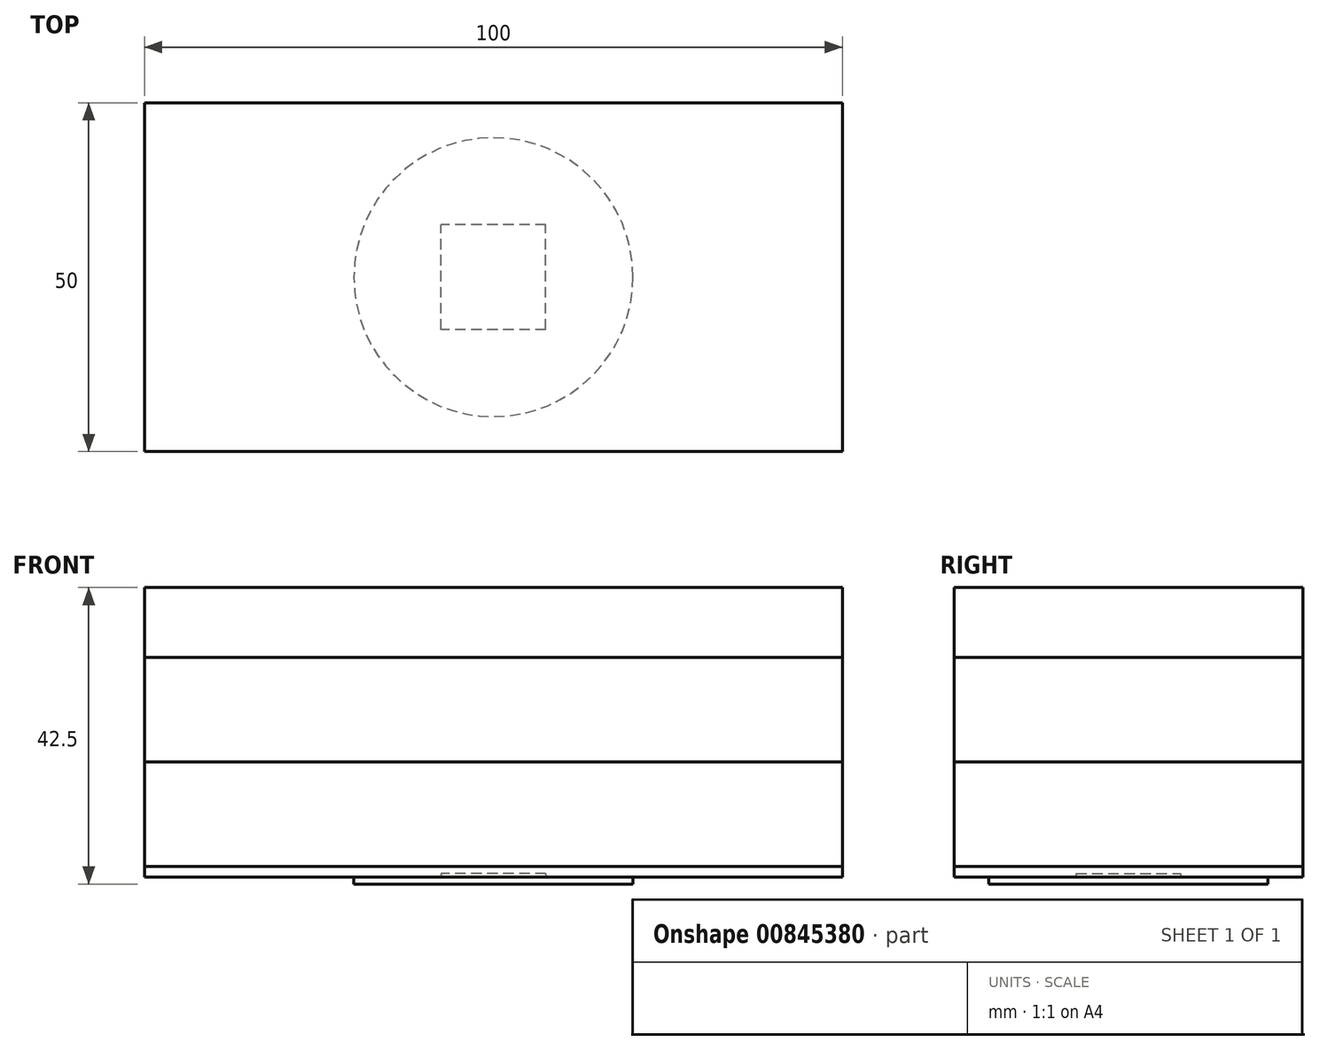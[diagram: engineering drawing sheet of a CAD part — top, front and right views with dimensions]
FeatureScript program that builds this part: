
annotation { "Feature Type Name" : "Feature", "Feature Type Description" : "" }
export const myFeature = defineFeature(function(context is Context, id is Id, definition is map)
    precondition{}
    {
        {
            var Q0;
            Q0=qCreatedBy(makeId("Top.planeOp"),FACE);
            var sketch = newSketch(context, id + "F0", { "sketchPlane" : qUnion([Q0])});
            skLineSegment(sketch, "E0.bottom", {"start": v(7.5, -7.5) * mm, "end": v(-7.5, -7.5) * mm});
            skLineSegment(sketch, "E0.top", {"start": v(7.5, 7.5) * mm, "end": v(-7.5, 7.5) * mm});
            skLineSegment(sketch, "E0.left", {"start": v(7.5, -7.5) * mm, "end": v(7.5, 7.5) * mm});
            skLineSegment(sketch, "E0.right", {"start": v(-7.5, -7.5) * mm, "end": v(-7.5, 7.5) * mm});
            skPoint(sketch, "E0.middle", {"position": v(0, 0) * mm});
            skSolve(sketch);
        }
        {
            var Q0;
            Q0 = qSketchRegion(id + "F0", true);
            extrude(context, id + "F1", {"entities" : qUnion([Q0]), "depth" : 0.5 * mm, "offsetDistance" : 25 * mm});
        }
        {
            var Q0;
            Q0=qCreatedBy(makeId("Top.planeOp"),FACE);
            var sketch = newSketch(context, id + "F2", { "sketchPlane" : qUnion([Q0])});
            skLineSegment(sketch, "E1.bottom", {"start": v(50, 25) * mm, "end": v(-50, 25) * mm});
            skLineSegment(sketch, "E1.top", {"start": v(50, -25) * mm, "end": v(-50, -25) * mm});
            skLineSegment(sketch, "E1.left", {"start": v(50, 25) * mm, "end": v(50, -25) * mm});
            skLineSegment(sketch, "E1.right", {"start": v(-50, 25) * mm, "end": v(-50, -25) * mm});
            skPoint(sketch, "E1.middle", {"position": v(0, 0) * mm});
            skSolve(sketch);
        }
        {
            var Q0;
            Q0 = qSketchRegion(id + "F2", true);
            extrude(context, id + "F3", {"entities" : qUnion([Q0]), "depth" : 1.5 * mm, "offsetDistance" : 25 * mm});
        }
        {
            var Q0;
            Q0=makeQuery(id+"F3.opExtrude","CAP_FACE",FACE,{"disambiguationData":[OSD([sQuery(id+"F2.wireOp",EDGE,"E1.bottom"),sQuery(id+"F2.wireOp",EDGE,"E1.top"),sQuery(id+"F2.wireOp",EDGE,"E1.left"),sQuery(id+"F2.wireOp",EDGE,"E1.right")])],"isStart":false});
            var sketch = newSketch(context, id + "F4", { "sketchPlane" : qUnion([Q0])});
            skLineSegment(sketch, "E2.bottom", {"start": v(-50, 25) * mm, "end": v(50, 25) * mm});
            skLineSegment(sketch, "E2.top", {"start": v(-50, -25) * mm, "end": v(50, -25) * mm});
            skLineSegment(sketch, "E2.left", {"start": v(-50, 25) * mm, "end": v(-50, -25) * mm});
            skLineSegment(sketch, "E2.right", {"start": v(50, 25) * mm, "end": v(50, -25) * mm});
            skPoint(sketch, "E2.middle", {"position": v(0, 0) * mm});
            skSolve(sketch);
        }
        {
            var Q0;
            Q0 = qSketchRegion(id + "F4", true);
            extrude(context, id + "F5", {"entities" : qUnion([Q0]), "depth" : 15 * mm, "offsetDistance" : 25 * mm});
        }
        {
            var Q0;
            Q0=makeQuery(id+"F5.opExtrude","CAP_FACE",FACE,{"disambiguationData":[OSD([sQuery(id+"F4.wireOp",EDGE,"E2.bottom"),sQuery(id+"F4.wireOp",EDGE,"E2.top"),sQuery(id+"F4.wireOp",EDGE,"E2.left"),sQuery(id+"F4.wireOp",EDGE,"E2.right")])],"isStart":false});
            var sketch = newSketch(context, id + "F6", { "sketchPlane" : qUnion([Q0])});
            skLineSegment(sketch, "E3.bottom", {"start": v(50, -25) * mm, "end": v(-50, -25) * mm});
            skLineSegment(sketch, "E3.top", {"start": v(50, 25) * mm, "end": v(-50, 25) * mm});
            skLineSegment(sketch, "E3.left", {"start": v(50, -25) * mm, "end": v(50, 25) * mm});
            skLineSegment(sketch, "E3.right", {"start": v(-50, -25) * mm, "end": v(-50, 25) * mm});
            skPoint(sketch, "E3.middle", {"position": v(0, 0) * mm});
            skSolve(sketch);
        }
        {
            var Q0;
            Q0 = qSketchRegion(id + "F6", true);
            extrude(context, id + "F7", {"entities" : qUnion([Q0]), "depth" : 15 * mm, "offsetDistance" : 25 * mm});
        }
        {
            var Q0;
            Q0=makeQuery(id+"F7.opExtrude","CAP_FACE",FACE,{"disambiguationData":[OSD([sQuery(id+"F6.wireOp",EDGE,"E3.bottom"),sQuery(id+"F6.wireOp",EDGE,"E3.top"),sQuery(id+"F6.wireOp",EDGE,"E3.left"),sQuery(id+"F6.wireOp",EDGE,"E3.right")])],"isStart":false});
            var sketch = newSketch(context, id + "F8", { "sketchPlane" : qUnion([Q0])});
            skLineSegment(sketch, "E4.bottom", {"start": v(-50, 25) * mm, "end": v(50, 25) * mm});
            skLineSegment(sketch, "E4.top", {"start": v(-50, -25) * mm, "end": v(50, -25) * mm});
            skLineSegment(sketch, "E4.left", {"start": v(-50, 25) * mm, "end": v(-50, -25) * mm});
            skLineSegment(sketch, "E4.right", {"start": v(50, 25) * mm, "end": v(50, -25) * mm});
            skPoint(sketch, "E4.middle", {"position": v(0, 0) * mm});
            skSolve(sketch);
        }
        {
            var Q0;
            Q0 = qSketchRegion(id + "F8", true);
            extrude(context, id + "F9", {"entities" : qUnion([Q0]), "depth" : 10 * mm, "offsetDistance" : 25 * mm});
        }
        {
            var Q0;
            Q0=makeQuery(id+"F1.opExtrude","CAP_FACE",FACE,{"disambiguationData":[OSD([sQuery(id+"F0.wireOp",EDGE,"E0.bottom"),sQuery(id+"F0.wireOp",EDGE,"E0.top"),sQuery(id+"F0.wireOp",EDGE,"E0.left"),sQuery(id+"F0.wireOp",EDGE,"E0.right")])],"isStart":true});
            var sketch = newSketch(context, id + "F10", { "sketchPlane" : qUnion([Q0])});
            skCircle(sketch, "E5", {"center": v(0, 0) * mm, "radius": 20 * mm});
            skSolve(sketch);
        }
        {
            var Q0;
            Q0 = qSketchRegion(id + "F10", true);
            extrude(context, id + "F11", {"entities" : qUnion([Q0]), "depth" : 1 * mm, "offsetDistance" : 25 * mm});
        }
    });
